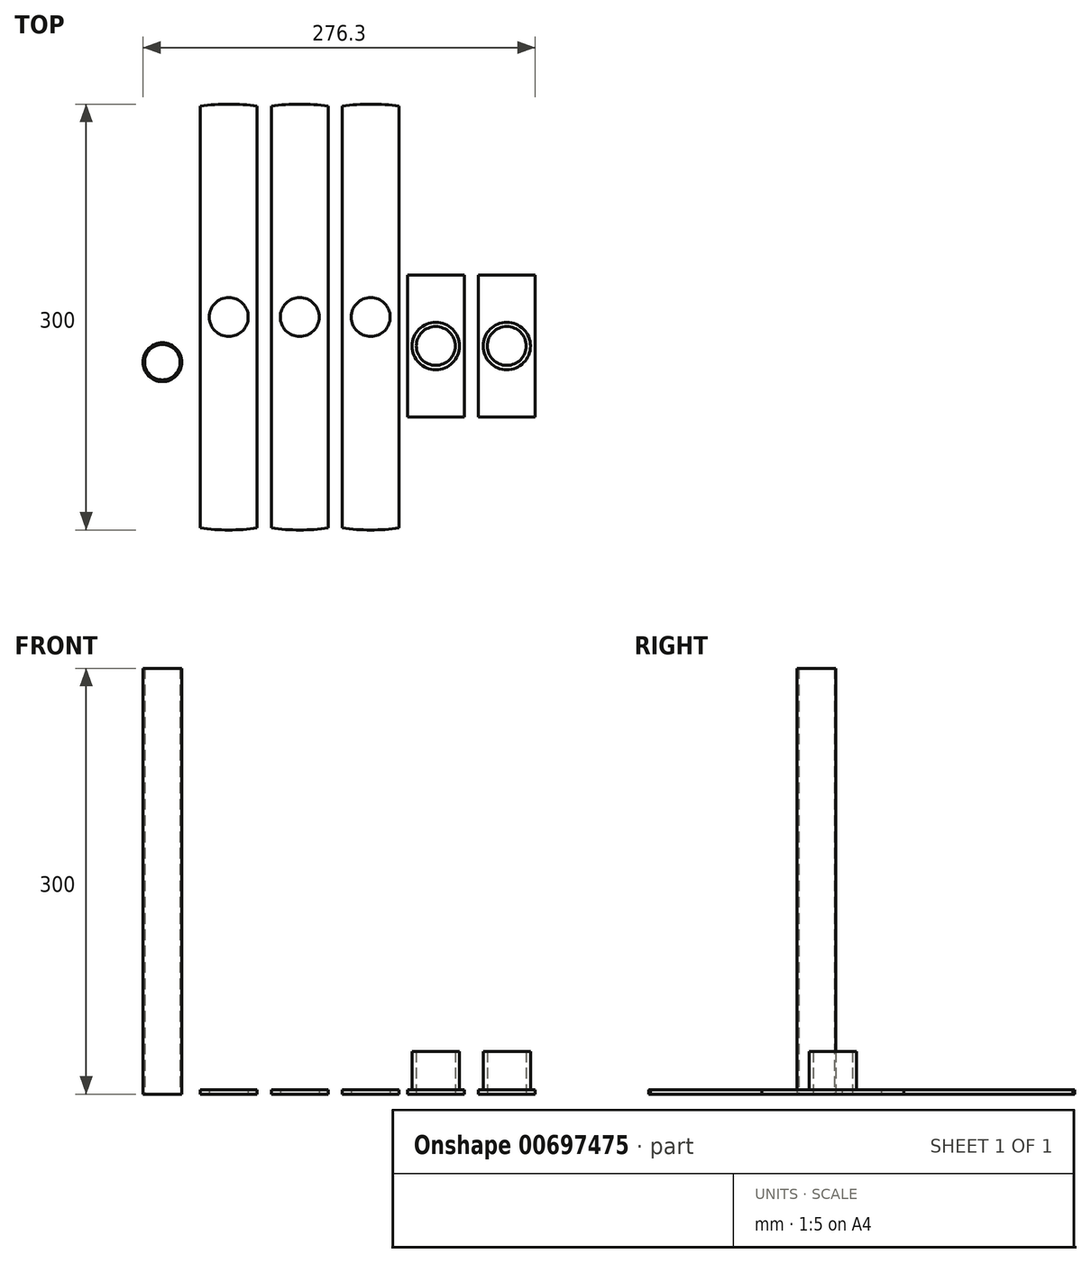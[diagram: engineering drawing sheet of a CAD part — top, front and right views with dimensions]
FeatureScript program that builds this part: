
annotation { "Feature Type Name" : "Feature", "Feature Type Description" : "" }
export const myFeature = defineFeature(function(context is Context, id is Id, definition is map)
    precondition{}
    {
        {
            assignVariable(context, id + "F0", {"name" : "Pipe_Length", "anyValue" : 300});
        }
        {
            assignVariable(context, id + "F1", {"name" : "Bar_Thickness", "anyValue" : 3});
        }
        {
            assignVariable(context, id + "F2", {"name" : "Flange_Height", "anyValue" : 30});
        }
        {
            var Q0;
            Q0=qCreatedBy(makeId("Top.planeOp"),FACE);
            var sketch = newSketch(context, id + "F3", { "sketchPlane" : qUnion([Q0])});
            skCircle(sketch, "E0", {"center": v(-31.44, 26.79) * mm, "radius": 13.7 * mm});
            skLineSegment(sketch, "E1", {"start": v(-31.44, 26.79) * mm, "end": v(-31.44, 13.09) * mm, "construction": true});
            skSolve(sketch);
        }
        {
            var Q0;
            Q0=qCreatedBy(makeId("Top.planeOp"),FACE);
            var sketch = newSketch(context, id + "F4", { "sketchPlane" : qUnion([Q0])});
            skCircle(sketch, "E2", {"center": v(-31.44, 26.79) * mm, "radius": 12.5 * mm});
            skLineSegment(sketch, "E3", {"start": v(-31.44, 26.79) * mm, "end": v(-31.44, 14.29) * mm, "construction": true});
            skSolve(sketch);
        }
        {
            var Q0;
            Q0 = qSketchRegion(id + "F3", true);
            extrude(context, id + "F5", {"entities" : qUnion([Q0]), "depth" : (getVariable(context, 'Pipe_Length')) * mm, "offsetDistance" : 25 * mm});
        }
        {
            var Q0;
            Q0 = qSketchRegion(id + "F4", true);
            extrude(context, id + "F6", {"entities" : qUnion([Q0]), "operationType" : NewBodyOperationType.REMOVE, "depth" : (getVariable(context, 'Pipe_Length')) * mm, "offsetDistance" : 25 * mm});
        }
        {
            var Q0;
            Q0=qCreatedBy(makeId("Top.planeOp"),FACE);
            var sketch = newSketch(context, id + "F7", { "sketchPlane" : qUnion([Q0])});
            skLineSegment(sketch, "E4.left", {"start": v(35.32, -90.08) * mm, "end": v(35.32, 207.24) * mm});
            skLineSegment(sketch, "E4.right", {"start": v(-4.68, -90.08) * mm, "end": v(-4.68, 207.24) * mm});
            skPoint(sketch, "E4.middle", {"position": v(15.32, 58.58) * mm});
            skArc(sketch, "E5", {"start": v(35.32, 207.24) * mm, "mid": v(15.32, 208.58) * mm, "end": v(-4.68, 207.24) * mm});
            skArc(sketch, "E6", {"start": v(-4.68, -90.08) * mm, "mid": v(15.32, -91.42) * mm, "end": v(35.32, -90.08) * mm});
            skLineSegment(sketch, "E7", {"start": v(15.32, 208.58) * mm, "end": v(15.32, -91.42) * mm, "construction": true});
            skSolve(sketch);
        }
        {
            var Q0;
            Q0=qCreatedBy(makeId("Top.planeOp"),FACE);
            var sketch = newSketch(context, id + "F8", { "sketchPlane" : qUnion([Q0])});
            skCircle(sketch, "E8", {"center": v(15.32, 58.58) * mm, "radius": 13.7 * mm});
            skLineSegment(sketch, "E9", {"start": v(15.32, 58.58) * mm, "end": v(15.32, 72.28) * mm, "construction": true});
            skSolve(sketch);
        }
        {
            var Q0;
            Q0 = qSketchRegion(id + "F7", true);
            extrude(context, id + "F9", {"entities" : qUnion([Q0]), "depth" : (getVariable(context, 'Bar_Thickness')) * mm, "offsetDistance" : 25 * mm});
        }
        {
            var Q0;
            Q0 = qSketchRegion(id + "F8", true);
            extrude(context, id + "F10", {"entities" : qUnion([Q0]), "operationType" : NewBodyOperationType.REMOVE, "depth" : (getVariable(context, 'Bar_Thickness')) * mm, "offsetDistance" : 25 * mm});
        }
        {
            var Q0;
            Q0=makeQuery(id+"F9.opExtrude","SWEPT_BODY",BODY,{"disambiguationData":[OSD([sQuery(id+"F7.wireOp",EDGE,"E4.left"),sQuery(id+"F7.wireOp",EDGE,"E4.right"),sQuery(id+"F7.wireOp",EDGE,"E5"),sQuery(id+"F7.wireOp",EDGE,"E6")])]});
            transform(context, id + "F11", {"entities" : qUnion([Q0]), "transformType" : TransformType.TRANSLATION_3D, "dx" : 50 * mm, "dy" : 0 * mm, "dz" : 0 * mm, "makeCopy" : true});
        }
        {
            var Q0;
            Q0=makeQuery(id+"F11.opPattern","COPY",BODY,{"derivedFrom":makeQuery(id+"F9.opExtrude","SWEPT_BODY",BODY,{"disambiguationData":[OSD([sQuery(id+"F7.wireOp",EDGE,"E4.left"),sQuery(id+"F7.wireOp",EDGE,"E4.right"),sQuery(id+"F7.wireOp",EDGE,"E5"),sQuery(id+"F7.wireOp",EDGE,"E6")])]}),"instanceName":"1"});
            transform(context, id + "F12", {"entities" : qUnion([Q0]), "transformType" : TransformType.TRANSLATION_3D, "dx" : 50 * mm, "dy" : 0 * mm, "dz" : 0 * mm, "makeCopy" : true});
        }
        {
            var Q0;
            Q0=qCreatedBy(makeId("Top.planeOp"),FACE);
            var sketch = newSketch(context, id + "F13", { "sketchPlane" : qUnion([Q0])});
            skLineSegment(sketch, "E10.bottom", {"start": v(181.16, 88.23) * mm, "end": v(141.16, 88.23) * mm});
            skLineSegment(sketch, "E10.top", {"start": v(181.16, -11.77) * mm, "end": v(141.16, -11.77) * mm});
            skLineSegment(sketch, "E10.left", {"start": v(181.16, 88.23) * mm, "end": v(181.16, -11.77) * mm});
            skLineSegment(sketch, "E10.right", {"start": v(141.16, 88.23) * mm, "end": v(141.16, -11.77) * mm});
            skPoint(sketch, "E10.middle", {"position": v(161.16, 38.23) * mm});
            skSolve(sketch);
        }
        {
            var Q0;
            Q0=qCreatedBy(makeId("Top.planeOp"),FACE);
            var sketch = newSketch(context, id + "F14", { "sketchPlane" : qUnion([Q0])});
            skCircle(sketch, "E11", {"center": v(161.16, 38.23) * mm, "radius": 16.7 * mm});
            skLineSegment(sketch, "E12", {"start": v(161.16, 38.23) * mm, "end": v(161.16, 54.93) * mm, "construction": true});
            skSolve(sketch);
        }
        {
            var Q0;
            Q0=qCreatedBy(makeId("Top.planeOp"),FACE);
            var sketch = newSketch(context, id + "F15", { "sketchPlane" : qUnion([Q0])});
            skCircle(sketch, "E13", {"center": v(161.16, 38.23) * mm, "radius": 13.7 * mm});
            skLineSegment(sketch, "E14", {"start": v(161.16, 38.23) * mm, "end": v(161.16, 51.93) * mm, "construction": true});
            skSolve(sketch);
        }
        {
            var Q0;
            Q0=makeQuery(id+"F13.imprint","IMPRINT",FACE,{"disambiguationData":[TD([[makeQuery(id+"F13.imprint","IMPRINT",EDGE,{"derivedFrom":sQuery(id+"F13.wireOp",EDGE,"E10.bottom")}),1.0]])]});
            extrude(context, id + "F16", {"entities" : qUnion([Q0]), "depth" : (getVariable(context, 'Bar_Thickness')) * mm, "offsetDistance" : 25 * mm});
        }
        {
            var Q0;
            Q0 = qSketchRegion(id + "F14", true);
            extrude(context, id + "F17", {"entities" : qUnion([Q0]), "operationType" : NewBodyOperationType.ADD, "depth" : (getVariable(context, 'Flange_Height')) * mm, "offsetDistance" : 25 * mm});
        }
        {
            var Q0;
            Q0 = qSketchRegion(id + "F15", true);
            extrude(context, id + "F18", {"entities" : qUnion([Q0]), "operationType" : NewBodyOperationType.REMOVE, "depth" : (getVariable(context, 'Flange_Height')) * mm, "offsetDistance" : 25 * mm});
        }
        {
            var Q0;
            Q0=makeQuery(id+"F16.opExtrude","SWEPT_BODY",BODY,{"disambiguationData":[OSD([sQuery(id+"F13.wireOp",EDGE,"E10.bottom"),sQuery(id+"F13.wireOp",EDGE,"E10.top"),sQuery(id+"F13.wireOp",EDGE,"E10.left"),sQuery(id+"F13.wireOp",EDGE,"E10.right")])]});
            transform(context, id + "F19", {"entities" : qUnion([Q0]), "transformType" : TransformType.TRANSLATION_3D, "dx" : 50 * mm, "dy" : 0 * mm, "dz" : 0 * mm, "makeCopy" : true});
        }
    });
